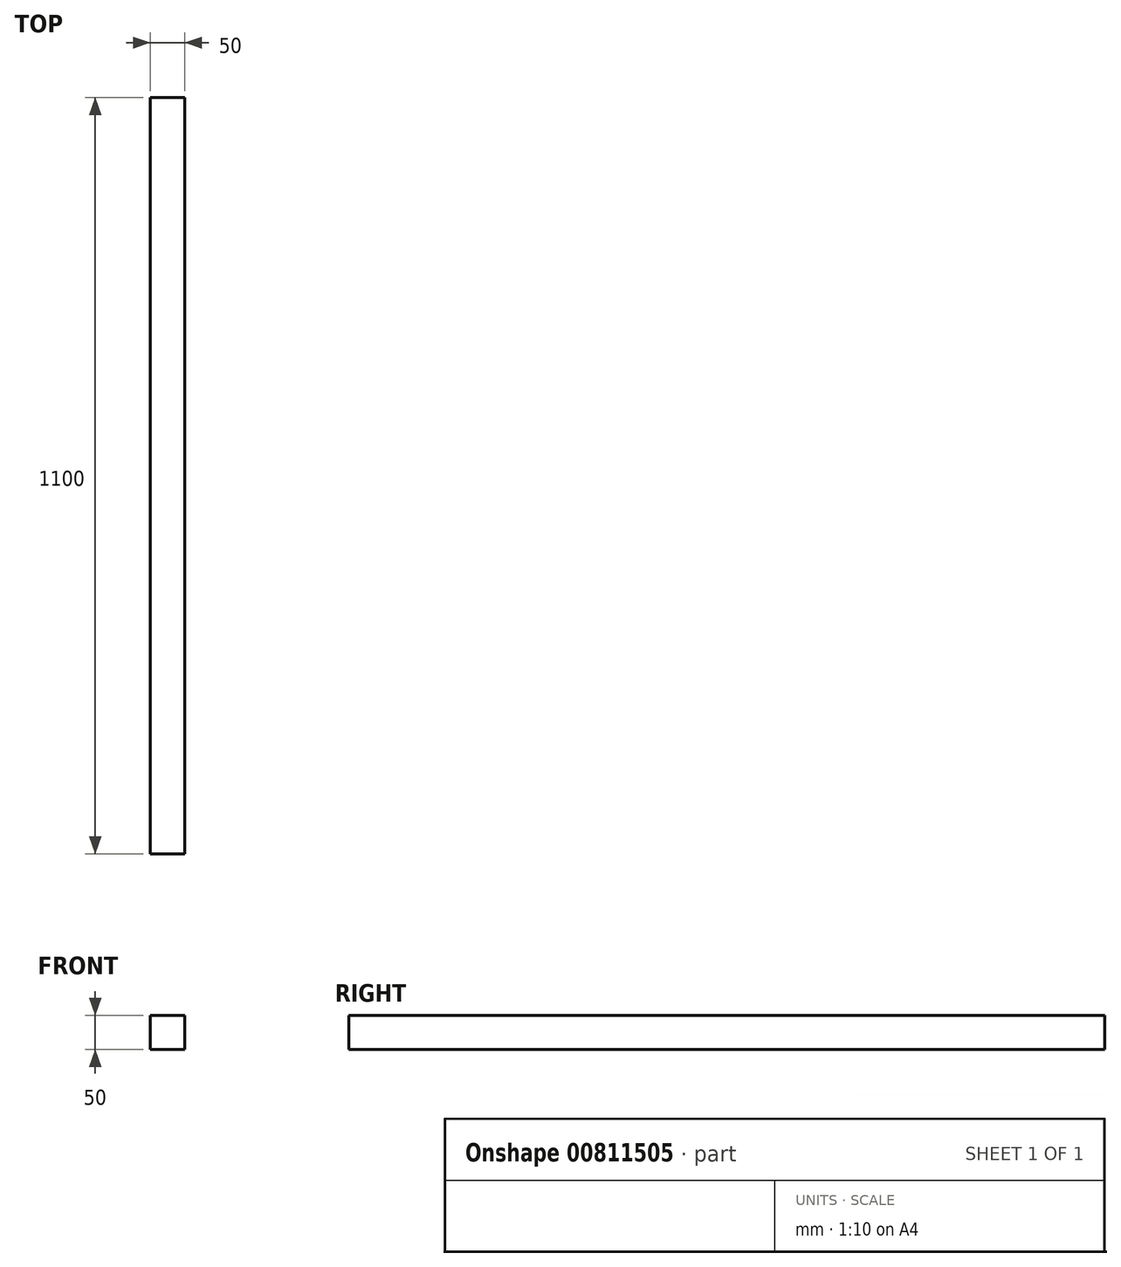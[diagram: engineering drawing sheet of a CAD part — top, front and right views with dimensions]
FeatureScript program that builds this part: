
annotation { "Feature Type Name" : "Feature", "Feature Type Description" : "" }
export const myFeature = defineFeature(function(context is Context, id is Id, definition is map)
    precondition{}
    {
        {
            var Q0;
            Q0=qCreatedBy(makeId("Front.planeOp"),FACE);
            var sketch = newSketch(context, id + "F0", { "sketchPlane" : qUnion([Q0])});
            skLineSegment(sketch, "E0.bottom", {"start": v(25, 25) * mm, "end": v(-25, 25) * mm});
            skLineSegment(sketch, "E0.top", {"start": v(25, -25) * mm, "end": v(-25, -25) * mm});
            skLineSegment(sketch, "E0.left", {"start": v(25, 25) * mm, "end": v(25, -25) * mm});
            skLineSegment(sketch, "E0.right", {"start": v(-25, 25) * mm, "end": v(-25, -25) * mm});
            skPoint(sketch, "E0.middle", {"position": v(0, 0) * mm});
            skSolve(sketch);
        }
        {
            var Q0;
            Q0=makeQuery(id+"F0.imprint","IMPRINT",FACE,{"disambiguationData":[TD([[makeQuery(id+"F0.imprint","IMPRINT",EDGE,{"derivedFrom":sQuery(id+"F0.wireOp",EDGE,"E0.bottom")}),1.0]])]});
            extrude(context, id + "F1", {"entities" : qUnion([Q0]), "endBound" : BoundingType.SYMMETRIC, "depth" : 1100 * mm, "offsetDistance" : 25.4 * mm});
        }
    });
